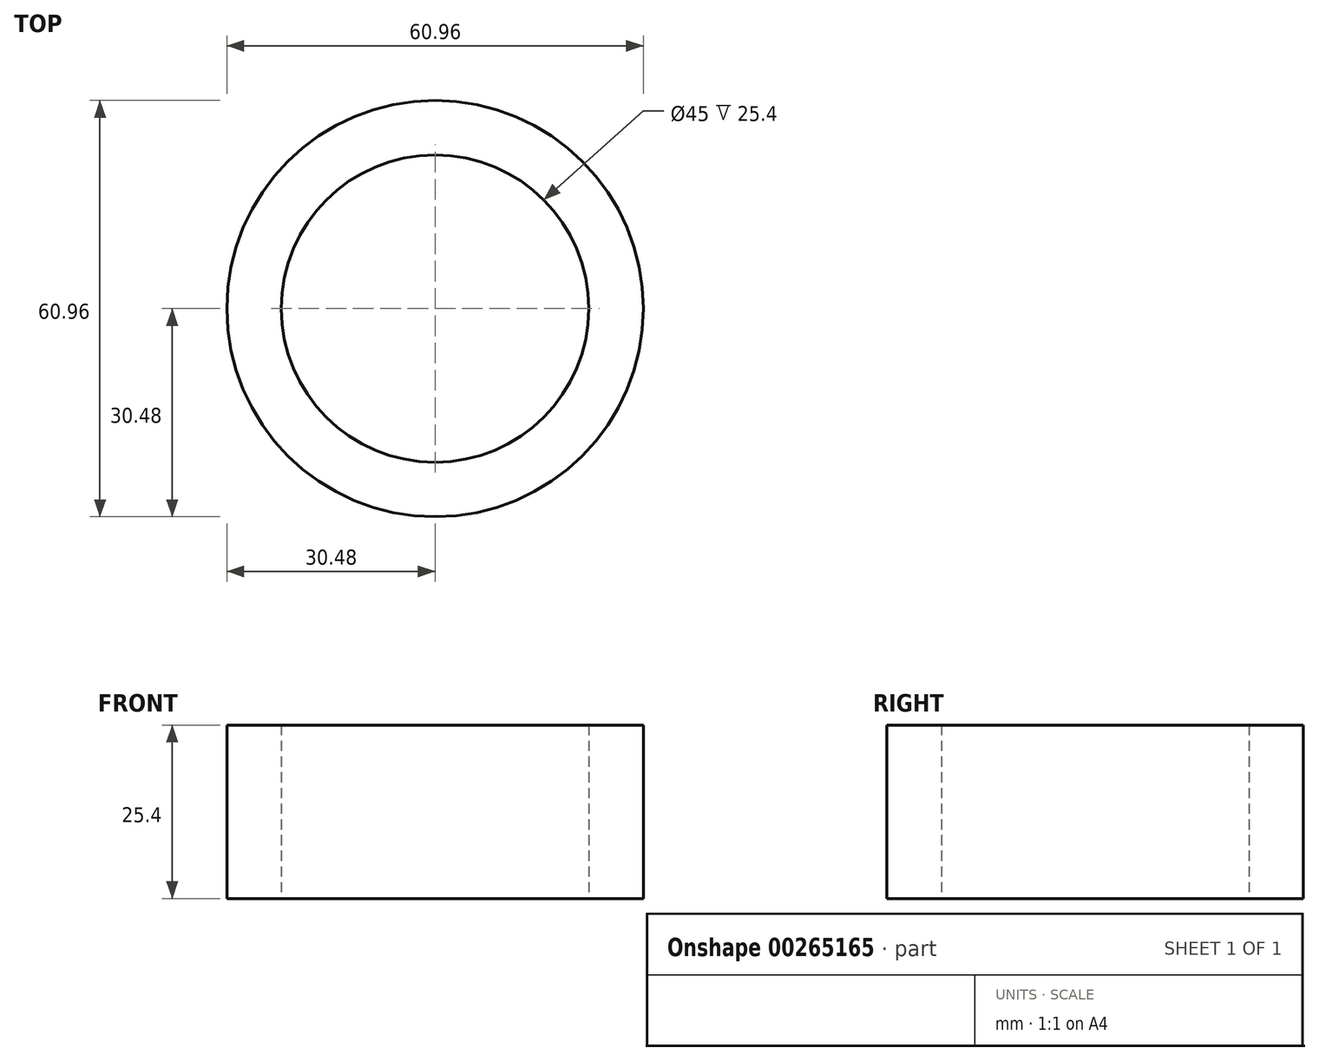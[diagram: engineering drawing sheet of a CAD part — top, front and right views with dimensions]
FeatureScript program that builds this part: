
annotation { "Feature Type Name" : "Feature", "Feature Type Description" : "" }
export const myFeature = defineFeature(function(context is Context, id is Id, definition is map)
    precondition{}
    {
        {
            var Q0;
            Q0=qCreatedBy(makeId("Top.planeOp"),FACE);
            var sketch = newSketch(context, id + "F0", { "sketchPlane" : qUnion([Q0])});
            skCircle(sketch, "E0", {"center": v(0, 0) * mm, "radius": 30.48 * mm});
            skCircle(sketch, "E1", {"center": v(0, 0) * mm, "radius": 22.5 * mm});
            skSolve(sketch);
        }
        {
            var Q0;
            Q0=makeQuery(id+"F0.imprint","IMPRINT",FACE,{"disambiguationData":[TD([[makeQuery(id+"F0.imprint","IMPRINT",EDGE,{"derivedFrom":sQuery(id+"F0.wireOp",EDGE,"E0")}),1.0]])]});
            extrude(context, id + "F1", {"entities" : qUnion([Q0]), "depth" : 25.4 * mm});
        }
    });
